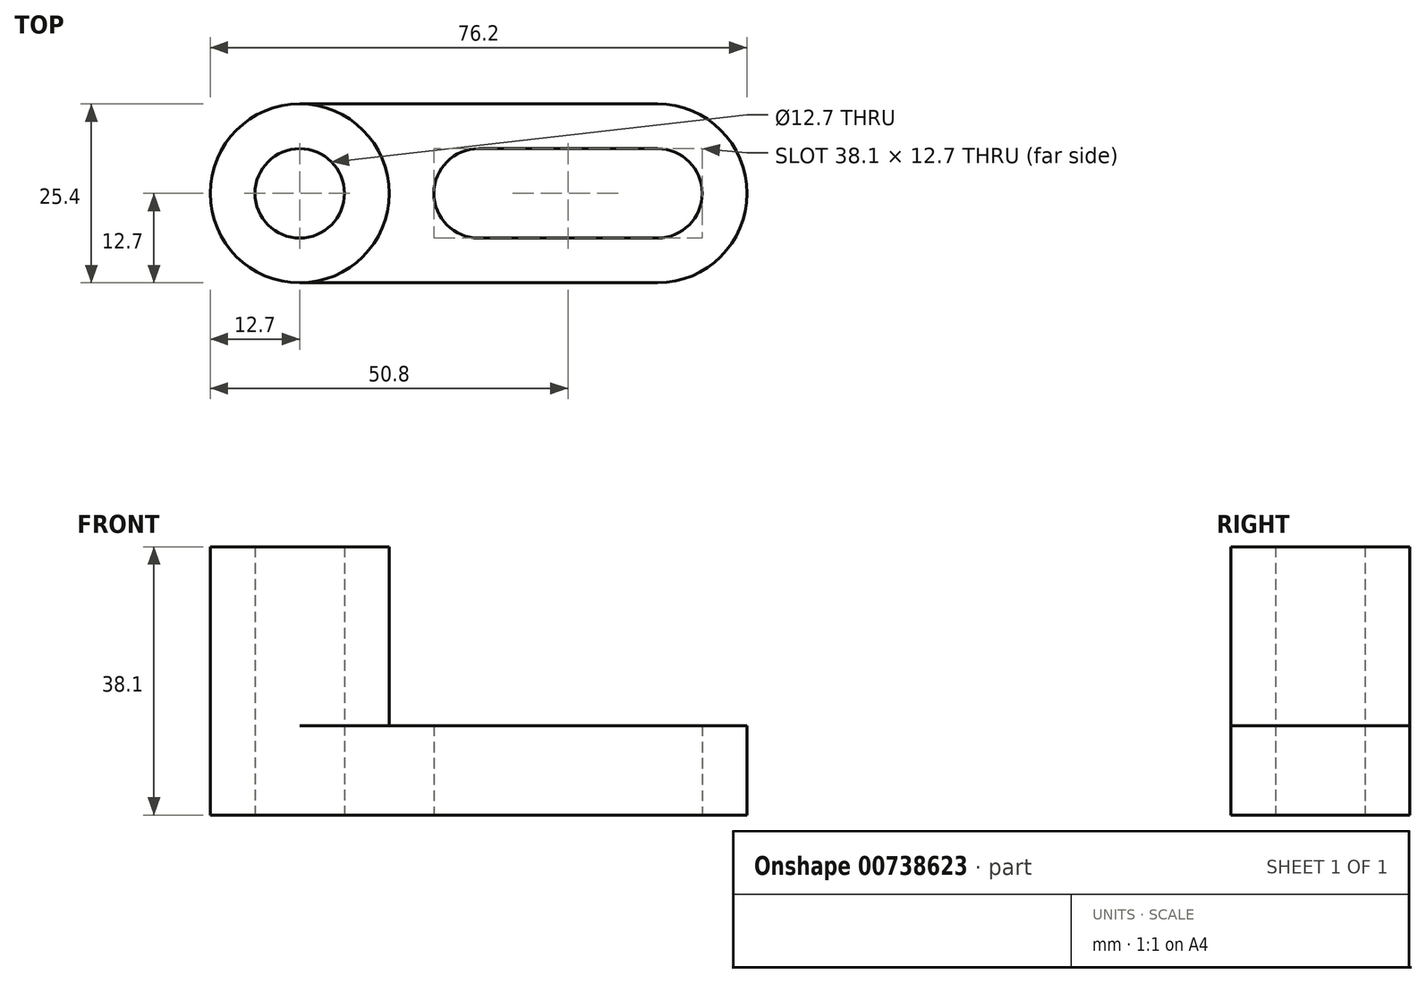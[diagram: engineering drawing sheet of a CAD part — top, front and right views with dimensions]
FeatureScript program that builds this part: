
annotation { "Feature Type Name" : "Feature", "Feature Type Description" : "" }
export const myFeature = defineFeature(function(context is Context, id is Id, definition is map)
    precondition{}
    {
        {
            var Q0;
            Q0=qCreatedBy(makeId("Top.planeOp"),FACE);
            var sketch = newSketch(context, id + "F0", { "sketchPlane" : qUnion([Q0])});
            skCircle(sketch, "E0", {"center": v(0, 0) * mm, "radius": 6.35 * mm});
            skCircle(sketch, "E1", {"center": v(0, 0) * mm, "radius": 12.7 * mm});
            skLineSegment(sketch, "E2", {"start": v(0, -12.7) * mm, "end": v(50.8, -12.7) * mm});
            skLineSegment(sketch, "E3", {"start": v(0, 12.7) * mm, "end": v(50.8, 12.7) * mm});
            skLineSegment(sketch, "E4", {"start": v(0, -12.7) * mm, "end": v(25.4, -12.7) * mm});
            skLineSegment(sketch, "E5", {"start": v(25.4, -12.7) * mm, "end": v(25.4, 0) * mm});
            skCircle(sketch, "E6", {"center": v(25.4, 0) * mm, "radius": 6.35 * mm});
            skLineSegment(sketch, "E7", {"start": v(50.8, 12.7) * mm, "end": v(50.8, 0) * mm});
            skCircle(sketch, "E8", {"center": v(50.8, 0) * mm, "radius": 6.35 * mm});
            skCircle(sketch, "E9", {"center": v(50.8, 0) * mm, "radius": 12.7 * mm});
            skLineSegment(sketch, "E10", {"start": v(25.4, -6.35) * mm, "end": v(50.8, -6.35) * mm});
            skLineSegment(sketch, "E11", {"start": v(25.4, 0) * mm, "end": v(25.4, 6.35) * mm});
            skLineSegment(sketch, "E12", {"start": v(25.4, 6.35) * mm, "end": v(50.8, 6.35) * mm});
            skSolve(sketch);
        }
        {
            var Q0;
            Q0=makeQuery(id+"F0.imprint","IMPRINT",FACE,{"disambiguationData":[TD([[makeQuery(id+"F0.imprint","IMPRINT",EDGE,{"derivedFrom":sQuery(id+"F0.wireOp",EDGE,"E0")}),-1.0]])]});
            var Q1;
            {var subQ4=sQuery(id+"F0.wireOp",EDGE,"E3");Q1=makeQuery(id+"F0.imprint","IMPRINT",FACE,{"disambiguationData":[TD([[makeQuery(id+"F0.imprint","IMPRINT",EDGE,{"derivedFrom":subQ4}),-1.0]])]});}
            var Q2;
            {var subQ0=sQuery(id+"F0.wireOp",EDGE,"E2");Q2=makeQuery(id+"F0.imprint","IMPRINT",FACE,{"disambiguationData":[TD([[makeQuery(id+"F0.imprint","IMPRINT",EDGE,{"derivedFrom":subQ0}),1.0]])]});}
            var Q3;
            {var subQ0=sQuery(id+"F0.wireOp",EDGE,"E9");var subQ1=makeQuery(id+"F0.imprint","INTERSECT",VERTEX,{"derivedFrom":[sQuery(id+"F0.wireOp",EDGE,"E2"),subQ0]});Q3=makeQuery(id+"F0.imprint","IMPRINT",FACE,{"disambiguationData":[TD([[makeQuery(id+"F0.imprint","IMPRINT",EDGE,{"disambiguationData":[TD([[subQ1,1.0]])],"derivedFrom":subQ0}),1.0]])]});}
            var Q4;
            {var subQ0=sQuery(id+"F0.wireOp",EDGE,"E9");var subQ3=sQuery(id+"F0.wireOp",EDGE,"E12");var subQ5=makeQuery(id+"F0.imprint","INTERSECT",VERTEX,{"derivedFrom":[subQ0,subQ3]});Q4=makeQuery(id+"F0.imprint","IMPRINT",FACE,{"disambiguationData":[TD([[makeQuery(id+"F0.imprint","IMPRINT",EDGE,{"disambiguationData":[TD([[subQ5,1.0]])],"derivedFrom":subQ0}),1.0]])]});}
            extrude(context, id + "F1", {"entities" : qUnion([Q0, Q1, Q2, Q3, Q4]), "depth" : 25.4 * mm, "offsetDistance" : 25.4 * mm});
        }
        {
            var Q0;
            Q0=makeQuery(id+"F1.opExtrude","CAP_FACE",FACE,{"disambiguationData":[OSD([sQuery(id+"F0.wireOp",EDGE,"E0"),sQuery(id+"F0.wireOp",EDGE,"E1"),sQuery(id+"F0.wireOp",EDGE,"E2"),sQuery(id+"F0.wireOp",EDGE,"E3"),sQuery(id+"F0.wireOp",EDGE,"E4"),sQuery(id+"F0.wireOp",EDGE,"E6"),sQuery(id+"F0.wireOp",EDGE,"E8"),sQuery(id+"F0.wireOp",EDGE,"E9"),sQuery(id+"F0.wireOp",EDGE,"E10"),sQuery(id+"F0.wireOp",EDGE,"E12")])],"isStart":false});
            var sketch = newSketch(context, id + "F2", { "sketchPlane" : qUnion([Q0])});
            skCircle(sketch, "E13", {"center": v(0, 0) * mm, "radius": 12.7 * mm});
            skSolve(sketch);
        }
        {
            var Q0;
            {var subQ0=makeQuery(id+"F1.opExtrude","CAP_EDGE",EDGE,{"disambiguationData":[OSD([sQuery(id+"F0.wireOp",EDGE,"E3")])],"isStart":false});Q0=makeQuery(id+"F2.imprint","IMPRINT",FACE,{"disambiguationData":[TD([[makeQuery(id+"F2.imprint","IMPRINT",EDGE,{"derivedFrom":subQ0}),-1.0]])]});}
            extrude(context, id + "F3", {"entities" : qUnion([Q0]), "operationType" : NewBodyOperationType.REMOVE, "oppositeDirection" : true, "depth" : 12.7 * mm, "offsetDistance" : 25.4 * mm});
        }
        {
            var Q0;
            Q0=makeQuery(id+"F1.opExtrude","CAP_FACE",FACE,{"disambiguationData":[OSD([sQuery(id+"F0.wireOp",EDGE,"E0"),sQuery(id+"F0.wireOp",EDGE,"E1"),sQuery(id+"F0.wireOp",EDGE,"E2"),sQuery(id+"F0.wireOp",EDGE,"E3"),sQuery(id+"F0.wireOp",EDGE,"E4"),sQuery(id+"F0.wireOp",EDGE,"E6"),sQuery(id+"F0.wireOp",EDGE,"E8"),sQuery(id+"F0.wireOp",EDGE,"E9"),sQuery(id+"F0.wireOp",EDGE,"E10"),sQuery(id+"F0.wireOp",EDGE,"E12")])],"isStart":false});
            extrude(context, id + "F4", {"entities" : qUnion([Q0]), "operationType" : NewBodyOperationType.ADD, "depth" : 12.7 * mm, "offsetDistance" : 25.4 * mm});
        }
    });
